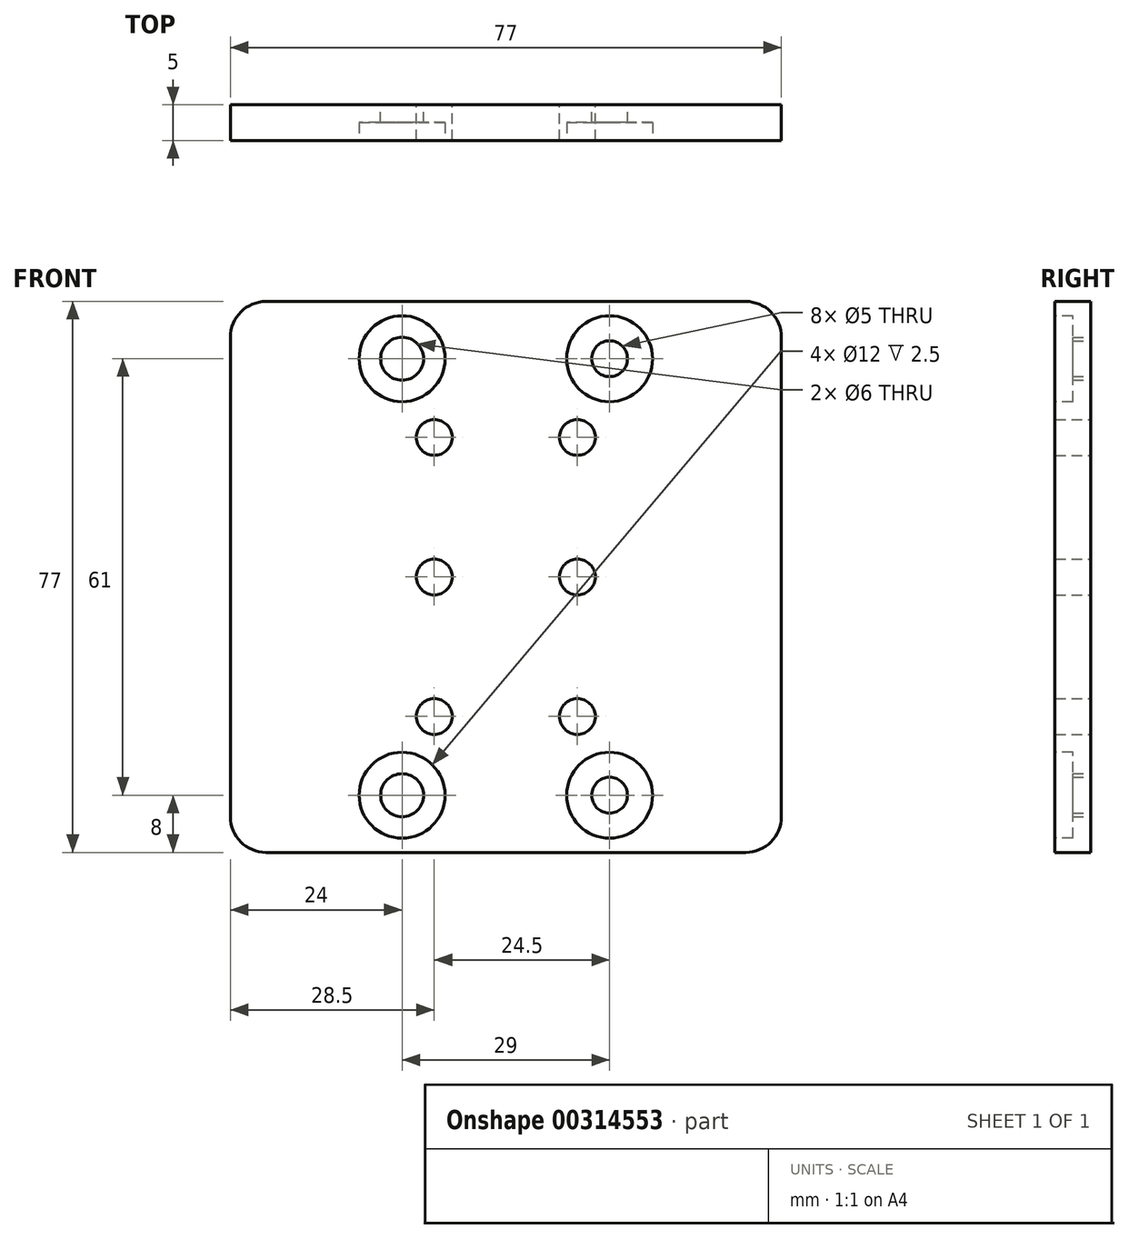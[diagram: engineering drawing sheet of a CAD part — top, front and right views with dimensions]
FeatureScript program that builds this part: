
annotation { "Feature Type Name" : "Feature", "Feature Type Description" : "" }
export const myFeature = defineFeature(function(context is Context, id is Id, definition is map)
    precondition{}
    {
        {
            var Q0;
            Q0=qCreatedBy(makeId("Front.planeOp"),FACE);
            var sketch = newSketch(context, id + "F0", { "sketchPlane" : qUnion([Q0])});
            skLineSegment(sketch, "E0.bottom", {"start": v(-33.5, -38.5) * mm, "end": v(33.5, -38.5) * mm});
            skLineSegment(sketch, "E0.top", {"start": v(-33.5, 38.5) * mm, "end": v(33.5, 38.5) * mm});
            skLineSegment(sketch, "E0.left", {"start": v(-38.5, -33.5) * mm, "end": v(-38.5, 33.5) * mm});
            skLineSegment(sketch, "E0.right", {"start": v(38.5, -33.5) * mm, "end": v(38.5, 33.5) * mm});
            skPoint(sketch, "E0.middle", {"position": v(0, 0) * mm});
            skPoint(sketch, "E1", {"position": v(-14.5, 30.5) * mm});
            skPoint(sketch, "E2", {"position": v(-10, 0) * mm});
            skPoint(sketch, "E3.MirrorP", {"position": v(-14.5, -30.5) * mm});
            skPoint(sketch, "E4.MirrorP", {"position": v(14.5, 30.5) * mm});
            skPoint(sketch, "E5.MirrorP", {"position": v(10, 0) * mm});
            skPoint(sketch, "E6.MirrorP", {"position": v(14.5, -30.5) * mm});
            skCircle(sketch, "E7", {"center": v(14.5, 30.5) * mm, "radius": 2.5 * mm});
            skCircle(sketch, "E8", {"center": v(14.5, -30.5) * mm, "radius": 2.5 * mm});
            skCircle(sketch, "E9", {"center": v(10, 0) * mm, "radius": 2.5 * mm});
            skCircle(sketch, "E10", {"center": v(-10, 0) * mm, "radius": 2.5 * mm});
            skCircle(sketch, "E11", {"center": v(-14.5, 30.5) * mm, "radius": 3 * mm});
            skCircle(sketch, "E12", {"center": v(-14.5, -30.5) * mm, "radius": 3 * mm});
            skPoint(sketch, "E13.visualSharp", {"position": v(-38.5, 38.5) * mm});
            skArc(sketch, "E13.filletArc", {"start": v(-33.5, 38.5) * mm, "mid": v(-37.04, 37.04) * mm, "end": v(-38.5, 33.5) * mm});
            skPoint(sketch, "E14.visualSharp", {"position": v(38.5, 38.5) * mm});
            skArc(sketch, "E14.filletArc", {"start": v(38.5, 33.5) * mm, "mid": v(37.04, 37.04) * mm, "end": v(33.5, 38.5) * mm});
            skPoint(sketch, "E15.visualSharp", {"position": v(38.5, -38.5) * mm});
            skArc(sketch, "E15.filletArc", {"start": v(33.5, -38.5) * mm, "mid": v(37.04, -37.04) * mm, "end": v(38.5, -33.5) * mm});
            skPoint(sketch, "E16.visualSharp", {"position": v(-38.5, -38.5) * mm});
            skArc(sketch, "E16.filletArc", {"start": v(-38.5, -33.5) * mm, "mid": v(-37.04, -37.04) * mm, "end": v(-33.5, -38.5) * mm});
            skPoint(sketch, "E17", {"position": v(-10, 19.5) * mm});
            skPoint(sketch, "E18.MirrorP", {"position": v(-10, -19.5) * mm});
            skPoint(sketch, "E19.MirrorP", {"position": v(10, 19.5) * mm});
            skPoint(sketch, "E20.MirrorP", {"position": v(10, -19.5) * mm});
            skCircle(sketch, "E21", {"center": v(-10, 19.5) * mm, "radius": 2.5 * mm});
            skCircle(sketch, "E22.MirrorC", {"center": v(-10, -19.5) * mm, "radius": 2.5 * mm});
            skCircle(sketch, "E23.MirrorC", {"center": v(10, 19.5) * mm, "radius": 2.5 * mm});
            skCircle(sketch, "E24.MirrorC", {"center": v(10, -19.5) * mm, "radius": 2.5 * mm});
            skSolve(sketch);
        }
        {
            var Q0;
            Q0 = qSketchRegion(id + "F0", true);
            extrude(context, id + "F1", {"entities" : qUnion([Q0]), "depth" : 5 * mm});
        }
        {
            var Q0;
            Q0=makeQuery(id+"F1.opExtrude","CAP_FACE",FACE,{"disambiguationData":[OSD([sQuery(id+"F0.wireOp",EDGE,"E0.bottom"),sQuery(id+"F0.wireOp",EDGE,"E0.top"),sQuery(id+"F0.wireOp",EDGE,"E0.left"),sQuery(id+"F0.wireOp",EDGE,"E0.right"),sQuery(id+"F0.wireOp",EDGE,"E7"),sQuery(id+"F0.wireOp",EDGE,"E8"),sQuery(id+"F0.wireOp",EDGE,"E9"),sQuery(id+"F0.wireOp",EDGE,"E10"),sQuery(id+"F0.wireOp",EDGE,"E11"),sQuery(id+"F0.wireOp",EDGE,"E12"),sQuery(id+"F0.wireOp",EDGE,"E13.filletArc"),sQuery(id+"F0.wireOp",EDGE,"E14.filletArc"),sQuery(id+"F0.wireOp",EDGE,"E15.filletArc"),sQuery(id+"F0.wireOp",EDGE,"E16.filletArc"),sQuery(id+"F0.wireOp",EDGE,"E21"),sQuery(id+"F0.wireOp",EDGE,"E22.MirrorC"),sQuery(id+"F0.wireOp",EDGE,"E23.MirrorC"),sQuery(id+"F0.wireOp",EDGE,"E24.MirrorC")])],"isStart":false});
            var sketch = newSketch(context, id + "F2", { "sketchPlane" : qUnion([Q0])});
            skCircle(sketch, "E25", {"center": v(-14.5, 30.5) * mm, "radius": 6 * mm});
            skCircle(sketch, "E26.MirrorC", {"center": v(-14.5, -30.5) * mm, "radius": 6 * mm});
            skCircle(sketch, "E27.MirrorC", {"center": v(14.5, 30.5) * mm, "radius": 6 * mm});
            skCircle(sketch, "E28.MirrorC", {"center": v(14.5, -30.5) * mm, "radius": 6 * mm});
            skSolve(sketch);
        }
        {
            var Q0;
            Q0 = qSketchRegion(id + "F2", true);
            extrude(context, id + "F3", {"entities" : qUnion([Q0]), "operationType" : NewBodyOperationType.REMOVE, "oppositeDirection" : true, "depth" : 2.5 * mm});
        }
    });
